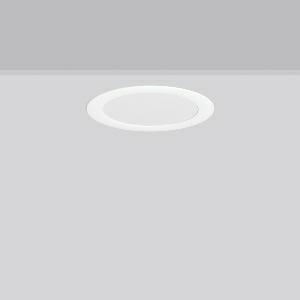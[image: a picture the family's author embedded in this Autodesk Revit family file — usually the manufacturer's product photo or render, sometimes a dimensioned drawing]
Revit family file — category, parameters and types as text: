
# Revit family: toledo_flat_round_672225_002_1_ce67
name_source: partatom
category: Lighting Fixtures
units: mm (PartAtom-declared; Revit-internal decimal feet)

## family parameters
Cut with Voids When Loaded = No
Host = Face
Light Source = No
Part Type = Normal
Room Calculation Point = No
Round Connector Dimension = Use Diameter
Shared = No

## types (1)
- TOLEDO FLAT round (1 x LED Modul 840, 1800 lm, 4000)
    Apparent Load = 17 VA
    CIE Flux Codes = 48 79 96 100 100
    Color Rendering = 80
    Color Temperature = 4000
    Default Elevation = 1800 mm  [stored 5.90551 ft]
    Description = Series: TOLEDO FLAT round
Ultra thin recessed downlight. For escape route illumination. Housing: die-cast aluminium, powder-coated. Lightguide and diffuser made of non-yellowing plastic (PMMA). Diffuser opal matt plastic. Ceiling installation with spring system. Including separate LED converter with connecting cable 250 mm. Self-contained system with automatic self-test. External driver with simple plug-in locking system. 
Colour: white
Diameter: 255 mm
Height: 3 mm
Cut-out diameter: 234 mm
Recess height: 100 mm
Luminaire: recess height: 60-80 mm
Weight: 1.76 kg
Operating mode: maintained power mode
Duration time: 8 h
Lamp: LED
Socket: without socket
Colour temperature: 4000K
Colour rendering index (CRI): 80
System power: 17 W
Rated luminous flux: 1800 lm
Luminous flux, emergency: 180 lm
System power, emergency: -
Control gear: Regulated power supply
Protection class: I
Type of protection: IP 54
    Height = 0 mm  [stored 0 ft]
    Lamp = 1 x LED Modul 840
    Lamp Light Flux = 1800 lm
    Lamp count = 1
    Length = 255 mm
    Lifetime = 50000 h
    Luminous efficacy = 106 lm/W
    Manufacturer = RZB
    ModVariant = No
    Model = 672225.002.1
    Mounting Place = Ceiling
    Mounting Type = Recessed
    Number of Poles = 1
    OnlyDefault = Yes
    Power Factor = 1
    Product Name = TOLEDO FLAT round
    Product group = Recessed downlights
    ProductGroupID = 402
    Protection Class = Protection class I
    Protection Degree = Degree of protection
    RLX_Detail_Level = 1
    RLX_Emergency_Light_Flux = 180 lm
    RLX_Emergency_Type = 3
    RLX_Emergency_Type_DB = Yes
    RlxData = <blob elided: 31097 chars, md5=85dfb2b5>
    Socket = socket
    Standby Power = 0 W
    System Light Flux = 1800 lm
    System Power = 17 W
    Type Comments = Product without accessories
    Type Image = 901453.002.jpg
    URL = http://relux.com
    VarID = ---
    Voltage = 0 V
    Weight = 0.00 kg
    Width = 0 mm  [stored 0 ft]

note: [stored X ft] marks values corroborated as IEEE doubles in the binary element streams (Revit-internal decimal feet)

## geometry (parser evidence)
native form markers: Blend x4, Sweep x11
no freeform markers — native parametric forms only
